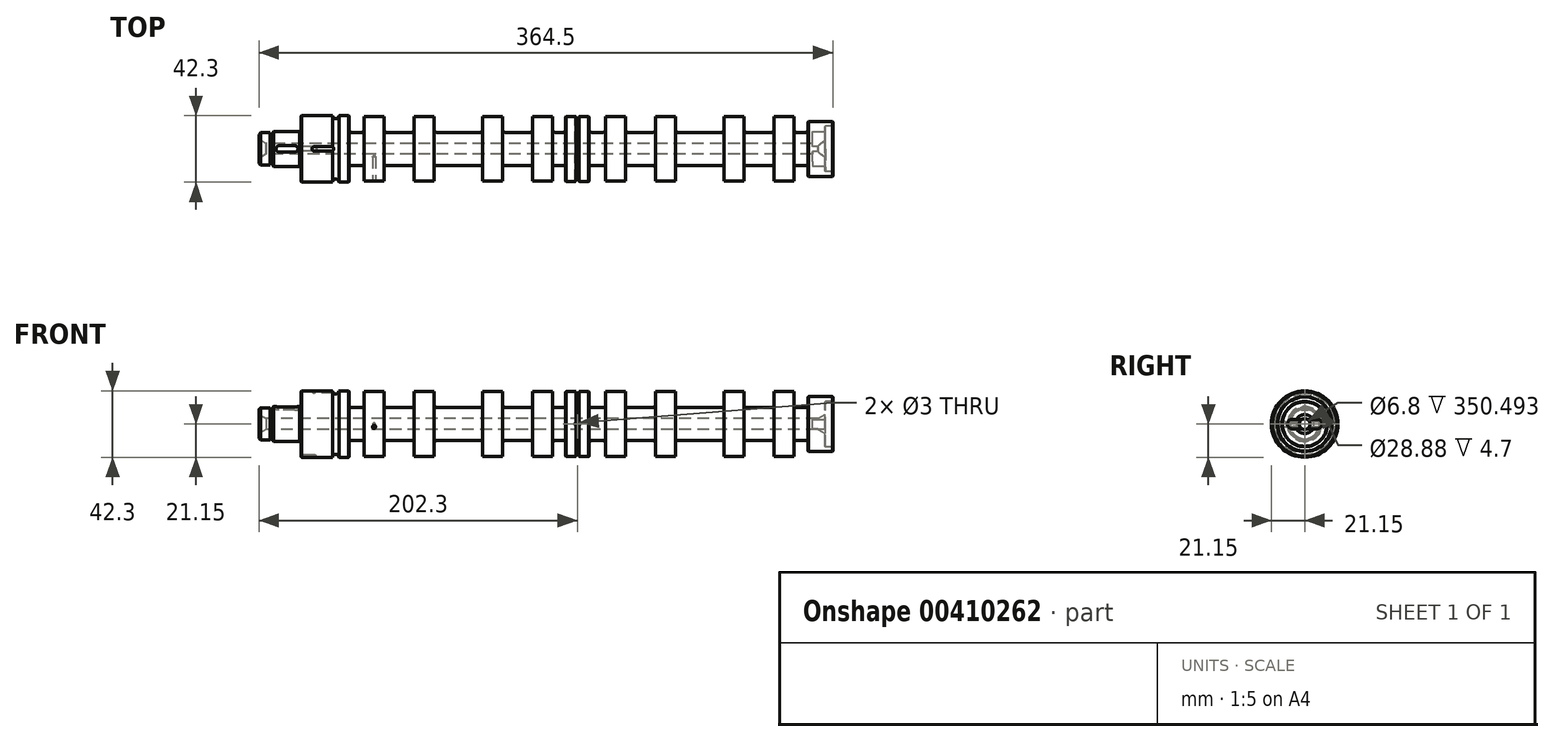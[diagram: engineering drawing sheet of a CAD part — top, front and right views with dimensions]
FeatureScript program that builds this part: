
annotation { "Feature Type Name" : "Feature", "Feature Type Description" : "" }
export const myFeature = defineFeature(function(context is Context, id is Id, definition is map)
    precondition{}
    {
        {
            var Q0;
            Q0=qCreatedBy(makeId("Front.planeOp"),FACE);
            var sketch = newSketch(context, id + "F0", { "sketchPlane" : qUnion([Q0])});
            skLineSegment(sketch, "E0", {"start": v(0, 0) * mm, "end": v(0, 10.23) * mm});
            skLineSegment(sketch, "E1", {"start": v(0, 10.23) * mm, "end": v(7.5, 10.23) * mm});
            skLineSegment(sketch, "E2", {"start": v(7.5, 10.23) * mm, "end": v(7.5, 9.4) * mm});
            skLineSegment(sketch, "E3", {"start": v(7.5, 9.4) * mm, "end": v(9, 9.4) * mm});
            skLineSegment(sketch, "E4", {"start": v(9, 9.4) * mm, "end": v(9, 11.1) * mm});
            skLineSegment(sketch, "E5", {"start": v(9, 11.1) * mm, "end": v(25.8, 11.1) * mm});
            skLineSegment(sketch, "E6", {"start": v(26.8, 11.1) * mm, "end": v(26.8, 21.15) * mm});
            skLineSegment(sketch, "E7", {"start": v(57.3, 21.15) * mm, "end": v(57.3, 10.5) * mm});
            skLineSegment(sketch, "E8", {"start": v(57.3, 10.5) * mm, "end": v(66.8, 10.5) * mm});
            skLineSegment(sketch, "E9", {"start": v(66.8, 10.5) * mm, "end": v(66.8, 20.55) * mm});
            skLineSegment(sketch, "E10", {"start": v(79.5, 20.55) * mm, "end": v(79.5, 10.5) * mm});
            skLineSegment(sketch, "E11", {"start": v(79.5, 10.5) * mm, "end": v(98.7, 10.5) * mm});
            skLineSegment(sketch, "E12", {"start": v(98.7, 10.5) * mm, "end": v(98.7, 20.55) * mm});
            skLineSegment(sketch, "E13", {"start": v(25.8, 11.1) * mm, "end": v(25.8, 10.6) * mm});
            skLineSegment(sketch, "E14", {"start": v(25.8, 10.6) * mm, "end": v(26.8, 10.6) * mm});
            skLineSegment(sketch, "E15", {"start": v(26.8, 10.6) * mm, "end": v(26.8, 11.1) * mm});
            skLineSegment(sketch, "E16.trimOffspring", {"start": v(50.8, 21.15) * mm, "end": v(57.3, 21.15) * mm});
            skLineSegment(sketch, "E17", {"start": v(111.4, 20.55) * mm, "end": v(111.4, 10.5) * mm});
            skLineSegment(sketch, "E18", {"start": v(111.4, 10.5) * mm, "end": v(142.2, 10.5) * mm});
            skLineSegment(sketch, "E19", {"start": v(142.2, 10.5) * mm, "end": v(142.2, 20.55) * mm});
            skLineSegment(sketch, "E20", {"start": v(154.9, 20.55) * mm, "end": v(154.9, 10.5) * mm});
            skLineSegment(sketch, "E21", {"start": v(154.9, 10.5) * mm, "end": v(173.9, 10.5) * mm});
            skLineSegment(sketch, "E22", {"start": v(173.9, 10.5) * mm, "end": v(173.9, 20.55) * mm});
            skLineSegment(sketch, "E23", {"start": v(186.6, 20.55) * mm, "end": v(186.6, 10.5) * mm});
            skLineSegment(sketch, "E24", {"start": v(186.6, 10.5) * mm, "end": v(194.8, 10.5) * mm});
            skLineSegment(sketch, "E25", {"start": v(194.8, 10.5) * mm, "end": v(194.8, 20.6) * mm});
            skLineSegment(sketch, "E26", {"start": v(194.8, 20.6) * mm, "end": v(201.3, 20.6) * mm});
            skLineSegment(sketch, "E27", {"start": v(203.3, 20.61) * mm, "end": v(209.8, 20.61) * mm});
            skLineSegment(sketch, "E28", {"start": v(209.8, 20.6) * mm, "end": v(209.8, 10.5) * mm});
            skArc(sketch, "E29", {"start": v(201.3, 20.6) * mm, "mid": v(202.3, 19.6) * mm, "end": v(203.3, 20.6) * mm});
            skLineSegment(sketch, "E30", {"start": v(0, 0) * mm, "end": v(359.5, 0) * mm});
            skLineSegment(sketch, "E31", {"start": v(186.6, 20.55) * mm, "end": v(173.9, 20.55) * mm});
            skLineSegment(sketch, "E32.trimOffspring", {"start": v(154.9, 20.55) * mm, "end": v(142.2, 20.55) * mm});
            skLineSegment(sketch, "E33.trimOffspring", {"start": v(111.4, 20.55) * mm, "end": v(98.7, 20.55) * mm});
            skLineSegment(sketch, "E34.trimOffspring", {"start": v(79.5, 20.55) * mm, "end": v(66.8, 20.55) * mm});
            skLineSegment(sketch, "E35", {"start": v(220.1, 10.5) * mm, "end": v(220.1, 20.55) * mm});
            skLineSegment(sketch, "E36", {"start": v(232.8, 20.55) * mm, "end": v(232.8, 10.5) * mm});
            skLineSegment(sketch, "E37", {"start": v(251.8, 10.5) * mm, "end": v(251.8, 20.55) * mm});
            skLineSegment(sketch, "E38", {"start": v(264.5, 20.55) * mm, "end": v(264.5, 10.5) * mm});
            skLineSegment(sketch, "E39", {"start": v(295.4, 10.5) * mm, "end": v(295.4, 20.55) * mm});
            skLineSegment(sketch, "E40", {"start": v(308.1, 20.55) * mm, "end": v(308.1, 10.5) * mm});
            skLineSegment(sketch, "E41", {"start": v(327.2, 10.5) * mm, "end": v(327.2, 20.55) * mm});
            skLineSegment(sketch, "E42", {"start": v(339.9, 20.55) * mm, "end": v(339.9, 10.5) * mm});
            skLineSegment(sketch, "E43", {"start": v(339.9, 20.55) * mm, "end": v(327.2, 20.55) * mm});
            skLineSegment(sketch, "E44.trimOffspring", {"start": v(308.1, 20.55) * mm, "end": v(295.4, 20.55) * mm});
            skLineSegment(sketch, "E45.trimOffspring", {"start": v(264.5, 20.55) * mm, "end": v(251.8, 20.55) * mm});
            skLineSegment(sketch, "E46.trimOffspring", {"start": v(232.8, 20.55) * mm, "end": v(220.1, 20.55) * mm});
            skLineSegment(sketch, "E47", {"start": v(348.8, 10.5) * mm, "end": v(348.8, 17.44) * mm});
            skLineSegment(sketch, "E48", {"start": v(348.8, 17.44) * mm, "end": v(364.5, 17.44) * mm});
            skLineSegment(sketch, "E49", {"start": v(359.5, 14.44) * mm, "end": v(359.5, 0) * mm});
            skLineSegment(sketch, "E50", {"start": v(46.8, 21.15) * mm, "end": v(26.8, 21.15) * mm});
            skArc(sketch, "E51", {"start": v(46.8, 21.15) * mm, "mid": v(48.8, 19.15) * mm, "end": v(50.8, 21.15) * mm});
            skLineSegment(sketch, "E52", {"start": v(209.8, 10.5) * mm, "end": v(220.1, 10.5) * mm});
            skLineSegment(sketch, "E53.trimOffspring", {"start": v(232.8, 10.5) * mm, "end": v(251.8, 10.5) * mm});
            skLineSegment(sketch, "E54.trimOffspring", {"start": v(264.5, 10.5) * mm, "end": v(295.4, 10.5) * mm});
            skLineSegment(sketch, "E55.trimOffspring", {"start": v(308.1, 10.5) * mm, "end": v(327.2, 10.5) * mm});
            skLineSegment(sketch, "E56.trimOffspring", {"start": v(339.9, 10.5) * mm, "end": v(348.8, 10.5) * mm});
            skLineSegment(sketch, "E57", {"start": v(359.5, 14.44) * mm, "end": v(364.5, 14.44) * mm});
            skLineSegment(sketch, "E58", {"start": v(364.5, 14.44) * mm, "end": v(364.5, 17.44) * mm});
            skSolve(sketch);
        }
        {
            var Q0;
            Q0=qSketchRegion(id+"F0",true);
            var Q1;
            Q1=sQuery(id+"F0.wireOp",EDGE,"E30");
            revolve(context, id + "F1", {"entities" : qUnion([Q0]), "axis" : qUnion([Q1]), "revolveType" : RevolveType.FULL});
        }
        {
            var Q0;
            Q0=makeQuery(id+"F1.opRevolve","SWEPT_EDGE",EDGE,{"disambiguationData":[OSD([sQuery(id+"F0.wireOp",EDGE,"E42"),sQuery(id+"F0.wireOp",EDGE,"E56.trimOffspring")])]});
            var Q1;
            Q1=makeQuery(id+"F1.opRevolve","SWEPT_EDGE",EDGE,{"disambiguationData":[OSD([sQuery(id+"F0.wireOp",EDGE,"E40"),sQuery(id+"F0.wireOp",EDGE,"E55.trimOffspring")])]});
            var Q2;
            Q2=makeQuery(id+"F1.opRevolve","SWEPT_EDGE",EDGE,{"disambiguationData":[OSD([sQuery(id+"F0.wireOp",EDGE,"E38"),sQuery(id+"F0.wireOp",EDGE,"E54.trimOffspring")])]});
            var Q3;
            Q3=makeQuery(id+"F1.opRevolve","SWEPT_EDGE",EDGE,{"disambiguationData":[OSD([sQuery(id+"F0.wireOp",EDGE,"E36"),sQuery(id+"F0.wireOp",EDGE,"E53.trimOffspring")])]});
            var Q4;
            Q4=makeQuery(id+"F1.opRevolve","SWEPT_EDGE",EDGE,{"disambiguationData":[OSD([sQuery(id+"F0.wireOp",EDGE,"E28"),sQuery(id+"F0.wireOp",EDGE,"E52")])]});
            var Q5;
            Q5=makeQuery(id+"F1.opRevolve","SWEPT_EDGE",EDGE,{"disambiguationData":[OSD([sQuery(id+"F0.wireOp",EDGE,"E23"),sQuery(id+"F0.wireOp",EDGE,"E24")])]});
            var Q6;
            Q6=makeQuery(id+"F1.opRevolve","SWEPT_EDGE",EDGE,{"disambiguationData":[OSD([sQuery(id+"F0.wireOp",EDGE,"E20"),sQuery(id+"F0.wireOp",EDGE,"E21")])]});
            var Q7;
            Q7=makeQuery(id+"F1.opRevolve","SWEPT_EDGE",EDGE,{"disambiguationData":[OSD([sQuery(id+"F0.wireOp",EDGE,"E17"),sQuery(id+"F0.wireOp",EDGE,"E18")])]});
            var Q8;
            Q8=makeQuery(id+"F1.opRevolve","SWEPT_EDGE",EDGE,{"disambiguationData":[OSD([sQuery(id+"F0.wireOp",EDGE,"E10"),sQuery(id+"F0.wireOp",EDGE,"E11")])]});
            var Q9;
            Q9=makeQuery(id+"F1.opRevolve","SWEPT_EDGE",EDGE,{"disambiguationData":[OSD([sQuery(id+"F0.wireOp",EDGE,"E7"),sQuery(id+"F0.wireOp",EDGE,"E8")])]});
            var Q10;
            Q10=makeQuery(id+"F1.opRevolve","SWEPT_EDGE",EDGE,{"disambiguationData":[OSD([sQuery(id+"F0.wireOp",EDGE,"E47"),sQuery(id+"F0.wireOp",EDGE,"E56.trimOffspring")])]});
            var Q11;
            Q11=makeQuery(id+"F1.opRevolve","SWEPT_EDGE",EDGE,{"disambiguationData":[OSD([sQuery(id+"F0.wireOp",EDGE,"E41"),sQuery(id+"F0.wireOp",EDGE,"E55.trimOffspring")])]});
            var Q12;
            Q12=makeQuery(id+"F1.opRevolve","SWEPT_EDGE",EDGE,{"disambiguationData":[OSD([sQuery(id+"F0.wireOp",EDGE,"E39"),sQuery(id+"F0.wireOp",EDGE,"E54.trimOffspring")])]});
            var Q13;
            Q13=makeQuery(id+"F1.opRevolve","SWEPT_EDGE",EDGE,{"disambiguationData":[OSD([sQuery(id+"F0.wireOp",EDGE,"E37"),sQuery(id+"F0.wireOp",EDGE,"E53.trimOffspring")])]});
            var Q14;
            Q14=makeQuery(id+"F1.opRevolve","SWEPT_EDGE",EDGE,{"disambiguationData":[OSD([sQuery(id+"F0.wireOp",EDGE,"E35"),sQuery(id+"F0.wireOp",EDGE,"E52")])]});
            var Q15;
            Q15=makeQuery(id+"F1.opRevolve","SWEPT_EDGE",EDGE,{"disambiguationData":[OSD([sQuery(id+"F0.wireOp",EDGE,"E21"),sQuery(id+"F0.wireOp",EDGE,"E22")])]});
            var Q16;
            Q16=makeQuery(id+"F1.opRevolve","SWEPT_EDGE",EDGE,{"disambiguationData":[OSD([sQuery(id+"F0.wireOp",EDGE,"E18"),sQuery(id+"F0.wireOp",EDGE,"E19")])]});
            var Q17;
            Q17=makeQuery(id+"F1.opRevolve","SWEPT_EDGE",EDGE,{"disambiguationData":[OSD([sQuery(id+"F0.wireOp",EDGE,"E11"),sQuery(id+"F0.wireOp",EDGE,"E12")])]});
            var Q18;
            Q18=makeQuery(id+"F1.opRevolve","SWEPT_EDGE",EDGE,{"disambiguationData":[OSD([sQuery(id+"F0.wireOp",EDGE,"E8"),sQuery(id+"F0.wireOp",EDGE,"E9")])]});
            var Q19;
            Q19=makeQuery(id+"F1.opRevolve","SWEPT_EDGE",EDGE,{"disambiguationData":[OSD([sQuery(id+"F0.wireOp",EDGE,"E24"),sQuery(id+"F0.wireOp",EDGE,"E25")])]});
            fillet(context, id + "F2", {"entities" : qUnion([Q0, Q1, Q2, Q3, Q4, Q5, Q6, Q7, Q8, Q9, Q10, Q11, Q12, Q13, Q14, Q15, Q16, Q17, Q18, Q19]), "radius" : 1.6 * mm, "tangentPropagation" : true, "allowEdgeOverflow" : false});
        }
        {
            var Q0;
            Q0=makeQuery(id+"F1.opRevolve","SWEPT_EDGE",EDGE,{"disambiguationData":[OSD([sQuery(id+"F0.wireOp",EDGE,"E0"),sQuery(id+"F0.wireOp",EDGE,"E1")])]});
            chamfer(context, id + "F3", {"entities" : qUnion([Q0]), "width" : 1 * mm, "tangentPropagation" : true});
        }
        {
            var Q0;
            Q0=makeQuery(id+"F1.opRevolve","SWEPT_EDGE",EDGE,{"disambiguationData":[OSD([sQuery(id+"F0.wireOp",EDGE,"E7"),sQuery(id+"F0.wireOp",EDGE,"E16.trimOffspring")])]});
            var Q1;
            Q1=makeQuery(id+"F1.opRevolve","SWEPT_EDGE",EDGE,{"disambiguationData":[OSD([sQuery(id+"F0.wireOp",EDGE,"E25"),sQuery(id+"F0.wireOp",EDGE,"E26")])]});
            var Q2;
            Q2=makeQuery(id+"F1.opRevolve","SWEPT_EDGE",EDGE,{"disambiguationData":[OSD([sQuery(id+"F0.wireOp",EDGE,"E27"),sQuery(id+"F0.wireOp",EDGE,"E28")])]});
            var Q3;
            Q3=makeQuery(id+"F1.opRevolve","SWEPT_EDGE",EDGE,{"disambiguationData":[OSD([sQuery(id+"F0.wireOp",EDGE,"E47"),sQuery(id+"F0.wireOp",EDGE,"E48")])]});
            var Q4;
            Q4=makeQuery(id+"F1.opRevolve","SWEPT_EDGE",EDGE,{"disambiguationData":[OSD([sQuery(id+"F0.wireOp",EDGE,"E48"),sQuery(id+"F0.wireOp",EDGE,"E49")])]});
            var Q5;
            Q5=makeQuery(id+"F1.opRevolve","SWEPT_EDGE",EDGE,{"disambiguationData":[OSD([sQuery(id+"F0.wireOp",EDGE,"E4"),sQuery(id+"F0.wireOp",EDGE,"E5")])]});
            var Q6;
            Q6=makeQuery(id+"F1.opRevolve","SWEPT_EDGE",EDGE,{"disambiguationData":[OSD([sQuery(id+"F0.wireOp",EDGE,"E6"),sQuery(id+"F0.wireOp",EDGE,"E50")])]});
            chamfer(context, id + "F4", {"entities" : qUnion([Q0, Q1, Q2, Q3, Q4, Q5, Q6]), "width" : 0.3 * mm, "tangentPropagation" : true});
        }
        {
            var Q0;
            Q0=makeQuery(id+"F1.opRevolve","SWEPT_EDGE",EDGE,{"disambiguationData":[OSD([sQuery(id+"F0.wireOp",EDGE,"E1"),sQuery(id+"F0.wireOp",EDGE,"E2")])]});
            chamfer(context, id + "F5", {"entities" : qUnion([Q0]), "chamferType" : ChamferType.OFFSET_ANGLE, "width" : 0.5 * mm, "oppositeDirection" : false, "angle" : 60 * degree, "tangentPropagation" : true});
        }
        {
            var Q0;
            Q0=makeQuery(id+"F1.opRevolve","SWEPT_EDGE",EDGE,{"disambiguationData":[OSD([sQuery(id+"F0.wireOp",EDGE,"E14"),sQuery(id+"F0.wireOp",EDGE,"E15")])]});
            var Q1;
            Q1=makeQuery(id+"F1.opRevolve","SWEPT_EDGE",EDGE,{"disambiguationData":[OSD([sQuery(id+"F0.wireOp",EDGE,"E13"),sQuery(id+"F0.wireOp",EDGE,"E14")])]});
            var Q2;
            Q2=makeQuery(id+"F1.opRevolve","SWEPT_EDGE",EDGE,{"disambiguationData":[OSD([sQuery(id+"F0.wireOp",EDGE,"E3"),sQuery(id+"F0.wireOp",EDGE,"E4")])]});
            var Q3;
            Q3=makeQuery(id+"F1.opRevolve","SWEPT_EDGE",EDGE,{"disambiguationData":[OSD([sQuery(id+"F0.wireOp",EDGE,"E2"),sQuery(id+"F0.wireOp",EDGE,"E3")])]});
            var Q4;
            Q4=makeQuery(id+"F5.opChamfer","BLEND_EDGE",EDGE,{"blendedFrom":[makeQuery(id+"F1.opRevolve","SWEPT_EDGE",EDGE,{"disambiguationData":[OSD([sQuery(id+"F0.wireOp",EDGE,"E1"),sQuery(id+"F0.wireOp",EDGE,"E2")])]}),makeQuery(id+"F1.opRevolve","SWEPT_FACE",FACE,{"disambiguationData":[OSD([sQuery(id+"F0.wireOp",EDGE,"E3")])]})],"blendedInto":[makeQuery(id+"F1.opRevolve","SWEPT_FACE",FACE,{"disambiguationData":[OSD([sQuery(id+"F0.wireOp",EDGE,"E3")])]})]});
            fillet(context, id + "F6", {"entities" : qUnion([Q0, Q1, Q2, Q3, Q4]), "radius" : 0.5 * mm, "tangentPropagation" : true, "allowEdgeOverflow" : false});
        }
        {
            var Q0;
            Q0=makeQuery(id+"F1.opRevolve","SWEPT_FACE",FACE,{"disambiguationData":[OSD([sQuery(id+"F0.wireOp",EDGE,"E49")])]});
            var sketch = newSketch(context, id + "F7", { "sketchPlane" : qUnion([Q0])});
            skLineSegment(sketch, "E59", {"start": v(-8, 3) * mm, "end": v(8, 3) * mm});
            skLineSegment(sketch, "E60", {"start": v(11, 0) * mm, "end": v(11, 0) * mm});
            skLineSegment(sketch, "E61", {"start": v(8, -3) * mm, "end": v(-8, -3) * mm});
            skLineSegment(sketch, "E62", {"start": v(-11, 0) * mm, "end": v(-11, 0) * mm});
            skPoint(sketch, "E63.visualSharp", {"position": v(-11, 3) * mm});
            skArc(sketch, "E63.filletArc", {"start": v(-8, 3) * mm, "mid": v(-10.12, 2.12) * mm, "end": v(-11, 0) * mm});
            skPoint(sketch, "E64.visualSharp", {"position": v(-11, -3) * mm});
            skArc(sketch, "E64.filletArc", {"start": v(-11, 0) * mm, "mid": v(-10.12, -2.12) * mm, "end": v(-8, -3) * mm});
            skPoint(sketch, "E65.visualSharp", {"position": v(11, 3) * mm});
            skArc(sketch, "E65.filletArc", {"start": v(11, 0) * mm, "mid": v(10.12, 2.12) * mm, "end": v(8, 3) * mm});
            skPoint(sketch, "E66.visualSharp", {"position": v(11, -3) * mm});
            skArc(sketch, "E66.filletArc", {"start": v(8, -3) * mm, "mid": v(10.12, -2.12) * mm, "end": v(11, 0) * mm});
            skSolve(sketch);
        }
        {
            var Q0;
            {var subQ1=sQuery(id+"F7.wireOp",EDGE,"E63.filletArc");Q0=makeQuery(id+"F7.imprint","IMPRINT",FACE,{"disambiguationData":[TD([[makeQuery(id+"F7.imprint","IMPRINT",EDGE,{"derivedFrom":subQ1}),1.0]])]});}
            var Q1;
            {var subQ1=sQuery(id+"F7.wireOp",EDGE,"E65.filletArc");Q1=makeQuery(id+"F7.imprint","IMPRINT",FACE,{"disambiguationData":[TD([[makeQuery(id+"F7.imprint","IMPRINT",EDGE,{"derivedFrom":subQ1}),1.0]])]});}
            var Q2;
            {var subQ0=sQuery(id+"F7.wireOp",EDGE,"E59");var subQ1=makeQuery(id+"F1.opRevolve","SWEPT_FACE",FACE,{"disambiguationData":[OSD([sQuery(id+"F0.wireOp",EDGE,"E49")])]});var subQ2=makeQuery(id+"FjbEp7hMja5GWEH_1.opChamfer","BLEND_EDGE",EDGE,{"blendedFrom":[makeQuery(id+"FVFhnxNaDeFgwCE_1.boolean.opBoolean","INTERSECT",EDGE,{"derivedFrom":[subQ1,makeQuery(id+"FVFhnxNaDeFgwCE_1.opExtrude","SWEPT_FACE",FACE,{"disambiguationData":[OSD([sQuery(id+"FgBfjt2P3U3ezcS_1.wireOp",EDGE,"Z8qlCyaP-uUiq-p7OV-OB7W-ui8Vbjvxlwgm")])]})]}),subQ1],"blendedInto":[subQ1]});var subQ3=makeQuery(id+"F7.imprint","INTERSECT",VERTEX,{"disambiguationData":[OD(0.0)],"derivedFrom":[subQ2,subQ0]});Q2=makeQuery(id+"F7.imprint","IMPRINT",FACE,{"disambiguationData":[TD([[makeQuery(id+"F7.imprint","IMPRINT",EDGE,{"disambiguationData":[TD([[subQ3,-1.0]])],"derivedFrom":subQ0}),-1.0]])]});}
            extrude(context, id + "F8", {"entities" : qUnion([Q0, Q1, Q2]), "operationType" : NewBodyOperationType.REMOVE, "oppositeDirection" : true, "depth" : 8 * mm});
        }
        {
            var Q0;
            Q0=qCreatedBy(makeId("Front.planeOp"),FACE);
            var sketch = newSketch(context, id + "F9", { "sketchPlane" : qUnion([Q0])});
            skLineSegment(sketch, "E67", {"start": v(33.8, 21.15) * mm, "end": v(33.8, 21.15) * mm});
            skLineSegment(sketch, "E68", {"start": v(35.3, 19.65) * mm, "end": v(48.8, 19.65) * mm});
            skLineSegment(sketch, "E69", {"start": v(48.8, 21.15) * mm, "end": v(48.8, 19.65) * mm});
            skPoint(sketch, "E70.visualSharp", {"position": v(33.8, 19.65) * mm});
            skArc(sketch, "E70.filletArc", {"start": v(33.8, 21.15) * mm, "mid": v(34.24, 20.09) * mm, "end": v(35.3, 19.65) * mm});
            skPoint(sketch, "E71.visualSharp", {"position": v(33.8, 22.64) * mm});
            skLineSegment(sketch, "E72", {"start": v(48.8, 21.15) * mm, "end": v(33.8, 21.15) * mm});
            skPoint(sketch, "E73.orphan", {"position": v(48.8, 22.65) * mm});
            skSolve(sketch);
        }
        {
            var Q0;
            Q0=makeQuery(id+"F9.imprint","IMPRINT",FACE,{"disambiguationData":[TD([[makeQuery(id+"F9.imprint","IMPRINT",EDGE,{"derivedFrom":sQuery(id+"F9.wireOp",EDGE,"E68")}),1.0]])]});
            var Q1;
            Q1=sQuery(id+"F9.wireOp",EDGE,"E72");
            revolve(context, id + "F10", {"operationType" : NewBodyOperationType.REMOVE, "entities" : qUnion([Q0]), "axis" : qUnion([Q1]), "revolveType" : RevolveType.FULL, "oppositeDirection" : true});
        }
        {
            var Q0;
            Q0=qCreatedBy(makeId("Front.planeOp"),FACE);
            var sketch = newSketch(context, id + "F11", { "sketchPlane" : qUnion([Q0])});
            skLineSegment(sketch, "E74", {"start": v(26.8, -19.65) * mm, "end": v(35.3, -19.65) * mm});
            skLineSegment(sketch, "E75", {"start": v(36.8, -21.15) * mm, "end": v(36.8, -21.15) * mm});
            skLineSegment(sketch, "E76", {"start": v(26.8, -21.15) * mm, "end": v(26.8, -19.65) * mm});
            skLineSegment(sketch, "E77", {"start": v(36.8, -21.15) * mm, "end": v(26.8, -21.15) * mm});
            skPoint(sketch, "E78.visualSharp", {"position": v(36.8, -19.65) * mm});
            skArc(sketch, "E78.filletArc", {"start": v(36.8, -21.15) * mm, "mid": v(36.36, -20.09) * mm, "end": v(35.3, -19.65) * mm});
            skSolve(sketch);
        }
        {
            var Q0;
            Q0=qSketchRegion(id+"F11",true);
            var Q1;
            Q1=sQuery(id+"F11.wireOp",EDGE,"E77");
            revolve(context, id + "F12", {"operationType" : NewBodyOperationType.REMOVE, "entities" : qUnion([Q0]), "axis" : qUnion([Q1]), "revolveType" : RevolveType.FULL, "oppositeDirection" : true});
        }
        {
            var Q0;
            Q0=qCreatedBy(makeId("Front.planeOp"),FACE);
            var sketch = newSketch(context, id + "F13", { "sketchPlane" : qUnion([Q0])});
            skCircle(sketch, "E79", {"center": v(202.3, 0) * mm, "radius": 1.5 * mm});
            skSolve(sketch);
        }
        {
            var Q0;
            Q0=qSketchRegion(id+"F13",true);
            extrude(context, id + "F14", {"entities" : qUnion([Q0]), "operationType" : NewBodyOperationType.REMOVE, "endBound" : BoundingType.SYMMETRIC, "depth" : 45 * mm, "offsetDistance" : 25 * mm});
        }
        {
            var Q0;
            Q0=qCreatedBy(makeId("Front.planeOp"),FACE);
            var sketch = newSketch(context, id + "F15", { "sketchPlane" : qUnion([Q0])});
            skLineSegment(sketch, "E80", {"start": v(10.8, 11.1) * mm, "end": v(24.8, 11.1) * mm});
            skLineSegment(sketch, "E81", {"start": v(24.8, 11.1) * mm, "end": v(24.8, 8.9) * mm});
            skLineSegment(sketch, "E82", {"start": v(24.8, 8.9) * mm, "end": v(10.8, 8.9) * mm});
            skLineSegment(sketch, "E83", {"start": v(10.8, 8.9) * mm, "end": v(10.8, 11.1) * mm});
            skSolve(sketch);
        }
        {
            var Q0;
            Q0=makeQuery(id+"F15.imprint","IMPRINT",FACE,{"disambiguationData":[TD([[makeQuery(id+"F15.imprint","IMPRINT",EDGE,{"derivedFrom":sQuery(id+"F15.wireOp",EDGE,"E80")}),-1.0]])]});
            extrude(context, id + "F16", {"entities" : qUnion([Q0]), "operationType" : NewBodyOperationType.REMOVE, "endBound" : BoundingType.SYMMETRIC, "depth" : 4 * mm});
        }
        {
            var Q0;
            Q0=makeQuery(id+"F16.boolean.opBoolean","COPY",EDGE,{"derivedFrom":makeQuery(id+"F16.opExtrude","CAP_EDGE",EDGE,{"disambiguationData":[OSD([sQuery(id+"F15.wireOp",EDGE,"E81")])],"isStart":true})});
            var Q1;
            Q1=makeQuery(id+"F16.boolean.opBoolean","COPY",EDGE,{"derivedFrom":makeQuery(id+"F16.opExtrude","CAP_EDGE",EDGE,{"disambiguationData":[OSD([sQuery(id+"F15.wireOp",EDGE,"E81")])],"isStart":false})});
            var Q2;
            Q2=makeQuery(id+"F16.boolean.opBoolean","COPY",EDGE,{"derivedFrom":makeQuery(id+"F16.opExtrude","CAP_EDGE",EDGE,{"disambiguationData":[OSD([sQuery(id+"F15.wireOp",EDGE,"E83")])],"isStart":true})});
            var Q3;
            Q3=makeQuery(id+"F16.boolean.opBoolean","COPY",EDGE,{"derivedFrom":makeQuery(id+"F16.opExtrude","CAP_EDGE",EDGE,{"disambiguationData":[OSD([sQuery(id+"F15.wireOp",EDGE,"E83")])],"isStart":false})});
            fillet(context, id + "F17", {"entities" : qUnion([Q0, Q1, Q2, Q3]), "radius" : 2 * mm, "tangentPropagation" : true, "allowEdgeOverflow" : false});
        }
        {
            var Q0;
            Q0=makeQuery(id+"F1.opRevolve","SWEPT_FACE",FACE,{"disambiguationData":[OSD([sQuery(id+"F0.wireOp",EDGE,"E0")])]});
            var sketch = newSketch(context, id + "F18", { "sketchPlane" : qUnion([Q0])});
            skPoint(sketch, "E84", {"position": v(0, 0) * mm});
            skSolve(sketch);
        }
        {
            var Q0;
            Q0=sQuery(id+"F18.wireOp",VERTEX,"E84");
            var Q1;
            Q1=makeQuery(id+"F1.opRevolve","SWEPT_BODY",BODY,{"disambiguationData":[OSD([sQuery(id+"F0.wireOp",EDGE,"E0"),sQuery(id+"F0.wireOp",EDGE,"E1"),sQuery(id+"F0.wireOp",EDGE,"E2"),sQuery(id+"F0.wireOp",EDGE,"E3"),sQuery(id+"F0.wireOp",EDGE,"E4"),sQuery(id+"F0.wireOp",EDGE,"E5"),sQuery(id+"F0.wireOp",EDGE,"E6"),sQuery(id+"F0.wireOp",EDGE,"E7"),sQuery(id+"F0.wireOp",EDGE,"E8"),sQuery(id+"F0.wireOp",EDGE,"E9"),sQuery(id+"F0.wireOp",EDGE,"E10"),sQuery(id+"F0.wireOp",EDGE,"E11"),sQuery(id+"F0.wireOp",EDGE,"E12"),sQuery(id+"F0.wireOp",EDGE,"E13"),sQuery(id+"F0.wireOp",EDGE,"E14"),sQuery(id+"F0.wireOp",EDGE,"E15"),sQuery(id+"F0.wireOp",EDGE,"E16.trimOffspring"),sQuery(id+"F0.wireOp",EDGE,"E17"),sQuery(id+"F0.wireOp",EDGE,"E18"),sQuery(id+"F0.wireOp",EDGE,"E19"),sQuery(id+"F0.wireOp",EDGE,"E20"),sQuery(id+"F0.wireOp",EDGE,"E21"),sQuery(id+"F0.wireOp",EDGE,"E22"),sQuery(id+"F0.wireOp",EDGE,"E23"),sQuery(id+"F0.wireOp",EDGE,"E24"),sQuery(id+"F0.wireOp",EDGE,"E25"),sQuery(id+"F0.wireOp",EDGE,"E26"),sQuery(id+"F0.wireOp",EDGE,"E27"),sQuery(id+"F0.wireOp",EDGE,"E28"),sQuery(id+"F0.wireOp",EDGE,"E29"),sQuery(id+"F0.wireOp",EDGE,"E30"),sQuery(id+"F0.wireOp",EDGE,"E31"),sQuery(id+"F0.wireOp",EDGE,"E32.trimOffspring"),sQuery(id+"F0.wireOp",EDGE,"E33.trimOffspring"),sQuery(id+"F0.wireOp",EDGE,"E34.trimOffspring"),sQuery(id+"F0.wireOp",EDGE,"E35"),sQuery(id+"F0.wireOp",EDGE,"E36"),sQuery(id+"F0.wireOp",EDGE,"E37"),sQuery(id+"F0.wireOp",EDGE,"E38"),sQuery(id+"F0.wireOp",EDGE,"E39"),sQuery(id+"F0.wireOp",EDGE,"E40"),sQuery(id+"F0.wireOp",EDGE,"E41"),sQuery(id+"F0.wireOp",EDGE,"E42"),sQuery(id+"F0.wireOp",EDGE,"E43"),sQuery(id+"F0.wireOp",EDGE,"E44.trimOffspring"),sQuery(id+"F0.wireOp",EDGE,"E45.trimOffspring"),sQuery(id+"F0.wireOp",EDGE,"E46.trimOffspring"),sQuery(id+"F0.wireOp",EDGE,"E47"),sQuery(id+"F0.wireOp",EDGE,"E48"),sQuery(id+"F0.wireOp",EDGE,"E49"),sQuery(id+"F0.wireOp",EDGE,"E50"),sQuery(id+"F0.wireOp",EDGE,"E51"),sQuery(id+"F0.wireOp",EDGE,"E52"),sQuery(id+"F0.wireOp",EDGE,"E53.trimOffspring"),sQuery(id+"F0.wireOp",EDGE,"E54.trimOffspring"),sQuery(id+"F0.wireOp",EDGE,"E55.trimOffspring"),sQuery(id+"F0.wireOp",EDGE,"E56.trimOffspring")])]});
            hole(context, id + "F19", {"style" : HoleStyle.C_SINK, "endStyle" : HoleEndStyle.THROUGH, "holeDiameter" : 6.8 * mm, "cSinkDiameter" : 12 * mm, "cSinkAngle" : 60 * degree, "tappedDepth" : 26.25 * mm, "tapClearance" : 3, "startFromSketch" : true, "locations" : qUnion([Q0]), "scope" : qUnion([Q1])});
        }
        {
            var Q0;
            Q0=makeQuery(id+"F1.opRevolve","SWEPT_FACE",FACE,{"disambiguationData":[OSD([sQuery(id+"F0.wireOp",EDGE,"E49")])]});
            var sketch = newSketch(context, id + "F20", { "sketchPlane" : qUnion([Q0])});
            skPoint(sketch, "E85", {"position": v(0, 0) * mm});
            skSolve(sketch);
        }
        {
            var Q0;
            Q0=sQuery(id+"F20.wireOp",VERTEX,"E85");
            var Q1;
            Q1=makeQuery(id+"F1.opRevolve","SWEPT_BODY",BODY,{"disambiguationData":[OSD([sQuery(id+"F0.wireOp",EDGE,"E0"),sQuery(id+"F0.wireOp",EDGE,"E1"),sQuery(id+"F0.wireOp",EDGE,"E2"),sQuery(id+"F0.wireOp",EDGE,"E3"),sQuery(id+"F0.wireOp",EDGE,"E4"),sQuery(id+"F0.wireOp",EDGE,"E5"),sQuery(id+"F0.wireOp",EDGE,"E6"),sQuery(id+"F0.wireOp",EDGE,"E7"),sQuery(id+"F0.wireOp",EDGE,"E8"),sQuery(id+"F0.wireOp",EDGE,"E9"),sQuery(id+"F0.wireOp",EDGE,"E10"),sQuery(id+"F0.wireOp",EDGE,"E11"),sQuery(id+"F0.wireOp",EDGE,"E12"),sQuery(id+"F0.wireOp",EDGE,"E13"),sQuery(id+"F0.wireOp",EDGE,"E14"),sQuery(id+"F0.wireOp",EDGE,"E15"),sQuery(id+"F0.wireOp",EDGE,"E16.trimOffspring"),sQuery(id+"F0.wireOp",EDGE,"E17"),sQuery(id+"F0.wireOp",EDGE,"E18"),sQuery(id+"F0.wireOp",EDGE,"E19"),sQuery(id+"F0.wireOp",EDGE,"E20"),sQuery(id+"F0.wireOp",EDGE,"E21"),sQuery(id+"F0.wireOp",EDGE,"E22"),sQuery(id+"F0.wireOp",EDGE,"E23"),sQuery(id+"F0.wireOp",EDGE,"E24"),sQuery(id+"F0.wireOp",EDGE,"E25"),sQuery(id+"F0.wireOp",EDGE,"E26"),sQuery(id+"F0.wireOp",EDGE,"E27"),sQuery(id+"F0.wireOp",EDGE,"E28"),sQuery(id+"F0.wireOp",EDGE,"E29"),sQuery(id+"F0.wireOp",EDGE,"E30"),sQuery(id+"F0.wireOp",EDGE,"E31"),sQuery(id+"F0.wireOp",EDGE,"E32.trimOffspring"),sQuery(id+"F0.wireOp",EDGE,"E33.trimOffspring"),sQuery(id+"F0.wireOp",EDGE,"E34.trimOffspring"),sQuery(id+"F0.wireOp",EDGE,"E35"),sQuery(id+"F0.wireOp",EDGE,"E36"),sQuery(id+"F0.wireOp",EDGE,"E37"),sQuery(id+"F0.wireOp",EDGE,"E38"),sQuery(id+"F0.wireOp",EDGE,"E39"),sQuery(id+"F0.wireOp",EDGE,"E40"),sQuery(id+"F0.wireOp",EDGE,"E41"),sQuery(id+"F0.wireOp",EDGE,"E42"),sQuery(id+"F0.wireOp",EDGE,"E43"),sQuery(id+"F0.wireOp",EDGE,"E44.trimOffspring"),sQuery(id+"F0.wireOp",EDGE,"E45.trimOffspring"),sQuery(id+"F0.wireOp",EDGE,"E46.trimOffspring"),sQuery(id+"F0.wireOp",EDGE,"E47"),sQuery(id+"F0.wireOp",EDGE,"E48"),sQuery(id+"F0.wireOp",EDGE,"E49"),sQuery(id+"F0.wireOp",EDGE,"E50"),sQuery(id+"F0.wireOp",EDGE,"E51"),sQuery(id+"F0.wireOp",EDGE,"E52"),sQuery(id+"F0.wireOp",EDGE,"E53.trimOffspring"),sQuery(id+"F0.wireOp",EDGE,"E54.trimOffspring"),sQuery(id+"F0.wireOp",EDGE,"E55.trimOffspring"),sQuery(id+"F0.wireOp",EDGE,"E56.trimOffspring")])]});
            hole(context, id + "F21", {"style" : HoleStyle.C_SINK, "endStyle" : HoleEndStyle.BLIND, "holeDiameter" : 6.8 * mm, "cSinkDiameter" : 12 * mm, "cSinkAngle" : 60 * degree, "holeDepth" : 30 * mm, "tappedDepth" : 26.25 * mm, "tapClearance" : 3, "startFromSketch" : true, "locations" : qUnion([Q0]), "scope" : qUnion([Q1]), "majorDiameter" : 5 * mm});
        }
        {
            var Q0;
            Q0=makeQuery(id+"F1.opRevolve","SWEPT_FACE",FACE,{"disambiguationData":[OSD([sQuery(id+"F0.wireOp",EDGE,"E49")])]});
            var sketch = newSketch(context, id + "F22", { "sketchPlane" : qUnion([Q0])});
            skCircle(sketch, "E86", {"center": v(0, 0) * mm, "radius": 25.83 * mm});
            skSolve(sketch);
        }
        {
            var Q0;
            Q0=makeQuery(id+"F1.opRevolve","SWEPT_FACE",FACE,{"disambiguationData":[OSD([sQuery(id+"F0.wireOp",EDGE,"E9")])]});
            cPlane(context, id + "F23", {"entities" : qUnion([Q0]), "cplaneType" : CPlaneType.OFFSET, "offset" : (12.7 / 2) * mm, "oppositeDirection" : true, "width" : 150 * mm, "height" : 150 * mm});
        }
        {
            var Q0;
            Q0=qCreatedBy(id+"F23.planeOp",FACE);
            var sketch = newSketch(context, id + "F24", { "sketchPlane" : qUnion([Q0])});
            skLineSegment(sketch, "E87", {"start": v(0, 0) * mm, "end": v(24.9, -2.18) * mm});
            skLineSegment(sketch, "E88", {"start": v(24.9, -2.18) * mm, "end": v(24.82, -3.18) * mm});
            skLineSegment(sketch, "E89", {"start": v(24.82, -3.18) * mm, "end": v(4.9, -1.43) * mm});
            skLineSegment(sketch, "E90", {"start": v(4.9, -1.43) * mm, "end": v(4.56, -0.75) * mm});
            skLineSegment(sketch, "E91", {"start": v(4.56, -0.75) * mm, "end": v(0, -0.35) * mm});
            skLineSegment(sketch, "E92", {"start": v(0, -0.35) * mm, "end": v(0, 0) * mm});
            skSolve(sketch);
        }
        {
            var Q0;
            Q0=makeQuery(id+"F24.imprint","IMPRINT",FACE,{"disambiguationData":[TD([[makeQuery(id+"F24.imprint","IMPRINT",EDGE,{"derivedFrom":sQuery(id+"F24.wireOp",EDGE,"E87")}),-1.0]])]});
            var Q1;
            Q1=sQuery(id+"F24.wireOp",EDGE,"E87");
            revolve(context, id + "F25", {"operationType" : NewBodyOperationType.REMOVE, "surfaceOperationType" : NewSurfaceOperationType.NEW, "entities" : qUnion([Q0]), "axis" : qUnion([Q1]), "revolveType" : RevolveType.FULL, "oppositeDirection" : true});
        }
    });
